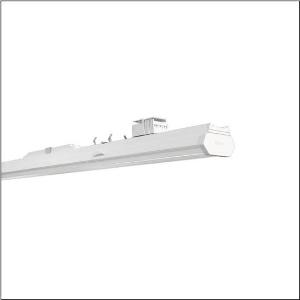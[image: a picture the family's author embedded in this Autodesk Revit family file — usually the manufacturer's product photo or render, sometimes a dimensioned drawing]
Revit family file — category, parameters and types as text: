
# Revit family: licross_r__11_protected_mo_51tp12dn495gd_6c21
name_source: partatom
category: Lighting Fixtures
units: mm (PartAtom-declared; Revit-internal decimal feet)

## family parameters
Cut with Voids When Loaded = No
Host = Face
Light Source = No
Part Type = Normal
Room Calculation Point = No
Round Connector Dimension = Use Diameter
Shared = No

## types (1)
- --- (1 x LED, 1500 lm, 9.3 W, 4000K)
    Apparent Load = 9 VA
    CIE Flux Codes = 73 92 98 99 100
    Color Rendering = 80
    Color Temperature = 4000K
    Default Elevation = 1800 mm
    Description = Licross® 11 Protected MO, luminaire insert, of sheet steel, galvanised, coil coated, white, length: 1.500mm, width: 90mm, height: 101mm, LED rated luminous flux: 9.980lm, light colour: 840, control gear: DALI 2, with plug, 6-pole, with phase selection, mains connection: 220..240V, AC/DC, 0/50..60Hz, rated input power: 57W, halogen-free wiring, for central battery installations according to DIN EN 60598-2-22, for emergency light function, without changeover relay, primary optical cover: cover, of PMMA, light emission: direct distribution, primary light characteristic: symmetric, protection rating (complete): IP64, insulation class (complete): insulation class I (protective earthing), certification: CE, ENEC, VDE, UKCA, protection symbol: D if used in an environment with conductive dust loads with corresponding accessories, impact resistance: IK06, permissible ambient temperature for indoor applications: -25..+35°C, standard: EN 60598-2-22, corresponds to IFS (International Featured Standards) requirements for safety and quality in the food industry, reducing of maximum allowable ambient temperature of 5°C with ceiling mounting, LABS conformity tested according to VDMA 24364:2018-05, packaging unit: 1 piece
    Height = 92 mm
    Lamp = 1 x LED
    Lamp Light Flux = 1500 lm
    Lamp Power = 9.3 W
    Lamp count = 1
    Length = 1500 mm  [stored 4.92126 ft]
    Luminous efficacy = 161 lm/W
    Manufacturer = Siteco
    ModVariant = No
    Model = 51TP12DN495GD
    Mounting Place = Ceiling
    Mounting Type = Pendant
    Number of Poles = 1
    OnlyDefault = Yes
    Power Factor = 1
    Product Name = Licross® 11 Protected MO
    Product group = luminaire insert
    ProductGroupID = 901
    Protection Class = Protection class I
    Protection Degree = IP 64
    RLX_Detail_Level = 1
    RLX_Emergency_Light_Flux = 0 lm
    RLX_Emergency_Type = 0
    RLX_Emergency_Type_DB = No
    RlxData = <blob elided: 24845 chars, md5=f01ece82>
    Socket = socket
    Standby Power = 0 W
    System Light Flux = 1500 lm
    System Power = 9 W
    Type Comments = : DC mode (central or group accumulator) initial emergency light level
    Type Image = l_1256148.jpg
    URL = http://relux.com
    VarID = @adj_038703
    Voltage = 0 V
    Weight = 0.00 kg
    Width = 88 mm

note: [stored X ft] marks values corroborated as IEEE doubles in the binary element streams (Revit-internal decimal feet)

## geometry (parser evidence)
native form markers: Blend x4, Sweep x10
no freeform markers — native parametric forms only
